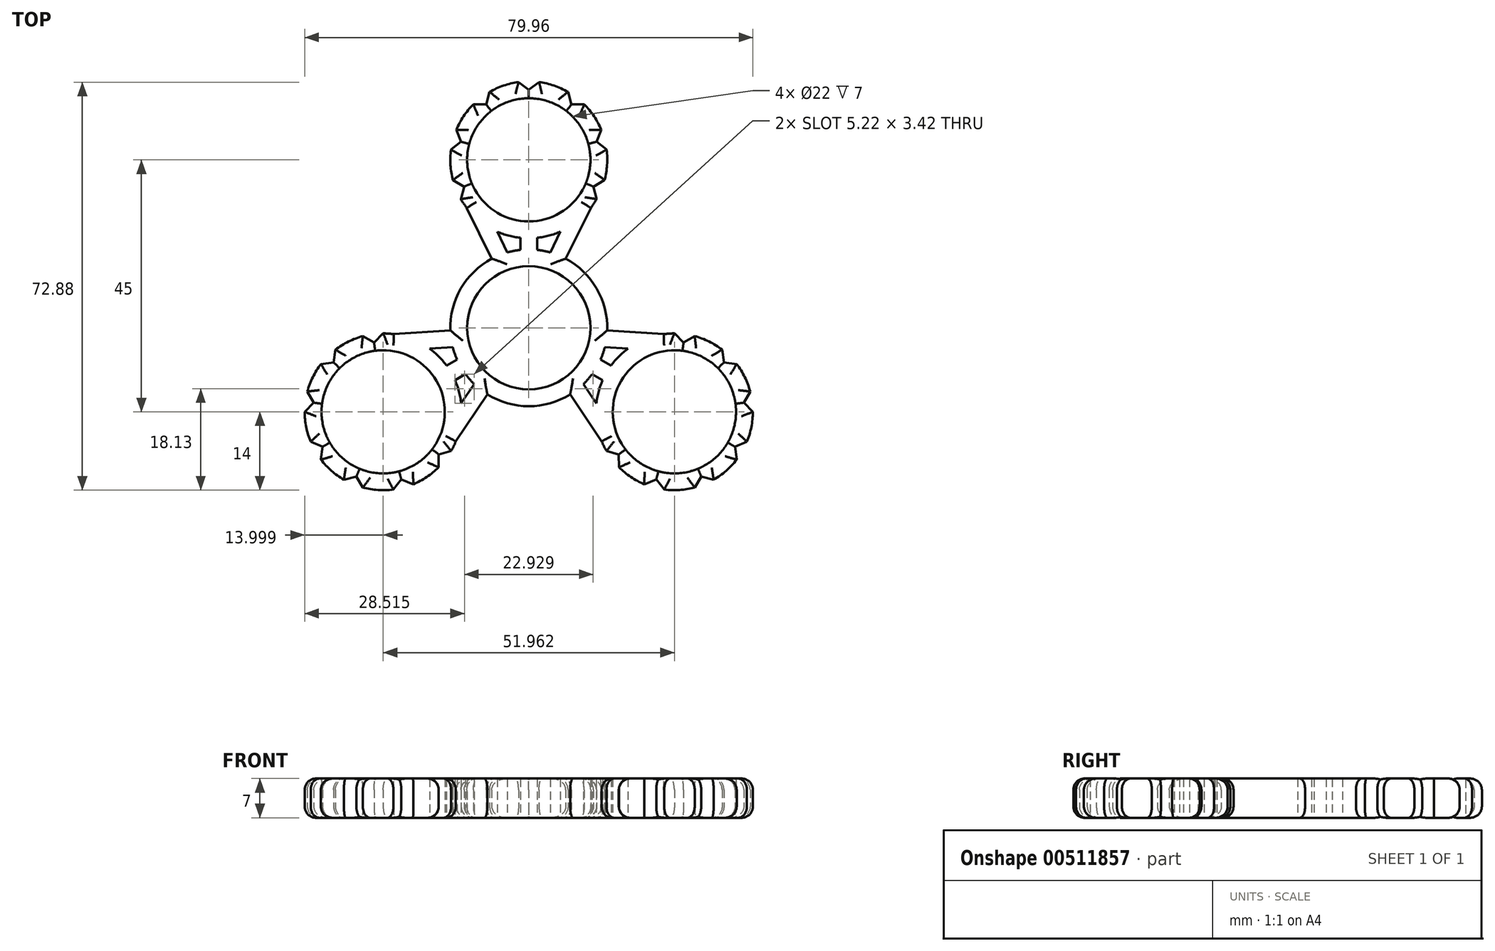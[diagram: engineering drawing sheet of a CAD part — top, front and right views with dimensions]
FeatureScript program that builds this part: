
annotation { "Feature Type Name" : "Feature", "Feature Type Description" : "" }
export const myFeature = defineFeature(function(context is Context, id is Id, definition is map)
    precondition{}
    {
        {
            var Q0;
            Q0=qCreatedBy(makeId("Top.planeOp"),FACE);
            var sketch = newSketch(context, id + "F0", { "sketchPlane" : qUnion([Q0])});
            skCircle(sketch, "E0", {"center": v(0, 0) * mm, "radius": 11 * mm});
            skCircle(sketch, "E1", {"center": v(0, 30) * mm, "radius": 11 * mm});
            skArc(sketch, "E2.0", {"start": v(-3.45, 16.43) * mm, "mid": v(9.84, 39.96) * mm, "end": v(-13.52, 26.38) * mm});
            skCircle(sketch, "E3.0", {"center": v(0, 0) * mm, "radius": 14 * mm});
            skLineSegment(sketch, "E4", {"start": v(-1.5, 15) * mm, "end": v(-1.5, 13.92) * mm});
            skLineSegment(sketch, "E5", {"start": v(-1.5, 15) * mm, "end": v(-1.5, 16.08) * mm});
            skPoint(sketch, "E6.MirrorCS.start.orphan", {"position": v(0, 15) * mm});
            skPoint(sketch, "E7.orphan", {"position": v(0, 16) * mm});
            skPoint(sketch, "E8.start.orphan", {"position": v(0, 14) * mm});
            skLineSegment(sketch, "E9.MirrorCS", {"start": v(1.5, 15) * mm, "end": v(1.5, 16.08) * mm});
            skLineSegment(sketch, "E10.MirrorCS", {"start": v(1.5, 15) * mm, "end": v(1.5, 13.92) * mm});
            skLineSegment(sketch, "E11", {"start": v(-9.53, 24.5) * mm, "end": v(-12.12, 23) * mm});
            skLineSegment(sketch, "E12", {"start": v(-10.63, 27.15) * mm, "end": v(-13.52, 26.38) * mm});
            skLineSegment(sketch, "E13", {"start": v(-12.12, 23) * mm, "end": v(-11.55, 25.22) * mm});
            skLineSegment(sketch, "E14", {"start": v(-11.55, 25.22) * mm, "end": v(-13.52, 26.38) * mm});
            skArc(sketch, "E15.trimOffspring", {"start": v(-12.12, 23) * mm, "mid": v(-11.62, 22.19) * mm, "end": v(-11.05, 21.4) * mm});
            skPoint(sketch, "E16.orphan", {"position": v(-12.93, 24.64) * mm});
            skPoint(sketch, "E17.start.orphan", {"position": v(-10.16, 25.8) * mm});
            skLineSegment(sketch, "E18.MirrorCS", {"start": v(9.53, 24.5) * mm, "end": v(12.12, 23) * mm});
            skLineSegment(sketch, "E19.1.0", {"start": v(-13.88, 31.83) * mm, "end": v(-12.07, 33.24) * mm});
            skLineSegment(sketch, "E19.1.1", {"start": v(-12.07, 33.24) * mm, "end": v(-12.93, 35.36) * mm});
            skLineSegment(sketch, "E19.2.0", {"start": v(-9.9, 39.9) * mm, "end": v(-7.6, 39.92) * mm});
            skLineSegment(sketch, "E19.2.1", {"start": v(-7.6, 39.92) * mm, "end": v(-7, 42.12) * mm});
            skLineSegment(sketch, "E19.3.0", {"start": v(-1.83, 43.88) * mm, "end": v(0, 42.5) * mm});
            skLineSegment(sketch, "E19.3.1", {"start": v(0, 42.5) * mm, "end": v(1.83, 43.88) * mm});
            skLineSegment(sketch, "E19.4.0", {"start": v(7, 42.12) * mm, "end": v(7.6, 39.92) * mm});
            skLineSegment(sketch, "E19.4.1", {"start": v(7.6, 39.92) * mm, "end": v(9.9, 39.9) * mm});
            skLineSegment(sketch, "E19.5.0", {"start": v(12.93, 35.36) * mm, "end": v(12.07, 33.24) * mm});
            skLineSegment(sketch, "E19.5.1", {"start": v(12.07, 33.24) * mm, "end": v(13.88, 31.83) * mm});
            skLineSegment(sketch, "E19.6.0", {"start": v(13.52, 26.38) * mm, "end": v(11.55, 25.22) * mm});
            skLineSegment(sketch, "E19.6.1", {"start": v(11.55, 25.22) * mm, "end": v(12.12, 23) * mm});
            skLineSegment(sketch, "E19.anchor1", {"start": v(0, 30) * mm, "end": v(-12.12, 23) * mm, "construction": true});
            skLineSegment(sketch, "E19.anchor2", {"start": v(0, 30) * mm, "end": v(13.52, 26.38) * mm, "construction": true});
            skLineSegment(sketch, "E20.MirrorCS", {"start": v(11.05, 21.4) * mm, "end": v(6.6, 12.34) * mm});
            skPoint(sketch, "E21.MirrorCS.end.orphan", {"position": v(11.05, 21.4) * mm});
            skPoint(sketch, "E21.MirrorCS.start.orphan", {"position": v(4.67, 13.2) * mm});
            skLineSegment(sketch, "E22", {"start": v(3.82, 13.47) * mm, "end": v(5.64, 17.19) * mm});
            skPoint(sketch, "E23.start.orphan", {"position": v(-4.67, 13.2) * mm});
            skPoint(sketch, "E24.end.orphan", {"position": v(-6.6, 12.34) * mm});
            skArc(sketch, "E25", {"start": v(-11.05, 21.4) * mm, "mid": v(-7.67, 18.29) * mm, "end": v(-3.45, 16.43) * mm});
            skLineSegment(sketch, "E26.MirrorCS", {"start": v(-3.82, 13.47) * mm, "end": v(-5.64, 17.19) * mm});
            skLineSegment(sketch, "E27.MirrorCS", {"start": v(-11.05, 21.4) * mm, "end": v(-6.6, 12.34) * mm});
            skPoint(sketch, "E28.MirrorCS.end.orphan", {"position": v(3.45, 16.43) * mm});
            skPoint(sketch, "E28.MirrorCS.start.orphan", {"position": v(1.5, 13.92) * mm});
            skLineSegment(sketch, "E29.1.0", {"start": v(-24.07, -1.13) * mm, "end": v(-14, -0.45) * mm});
            skLineSegment(sketch, "E29.1.1", {"start": v(-13.57, -3.42) * mm, "end": v(-17.7, -3.7) * mm});
            skArc(sketch, "E29.1.2", {"start": v(-12.5, -11.2) * mm, "mid": v(-39.53, -11.46) * mm, "end": v(-16.08, -24.9) * mm});
            skLineSegment(sketch, "E29.1.3", {"start": v(-13.74, -6.2) * mm, "end": v(-12.8, -5.66) * mm});
            skLineSegment(sketch, "E29.1.4", {"start": v(-13.74, -6.2) * mm, "end": v(-14.68, -6.74) * mm});
            skLineSegment(sketch, "E29.1.5", {"start": v(-12.24, -8.8) * mm, "end": v(-13.18, -9.34) * mm});
            skLineSegment(sketch, "E29.1.6", {"start": v(-12.24, -8.8) * mm, "end": v(-11.3, -8.26) * mm});
            skArc(sketch, "E29.1.7", {"start": v(-13.01, -20.28) * mm, "mid": v(-12, -15.78) * mm, "end": v(-12.5, -11.2) * mm});
            skLineSegment(sketch, "E29.1.8", {"start": v(-13.01, -20.28) * mm, "end": v(-7.38, -11.9) * mm});
            skLineSegment(sketch, "E29.1.9", {"start": v(-9.75, -10.04) * mm, "end": v(-12.06, -13.48) * mm});
            skLineSegment(sketch, "E29.1.10", {"start": v(-13.86, -22) * mm, "end": v(-16.06, -22.6) * mm});
            skLineSegment(sketch, "E29.1.11", {"start": v(-16.06, -22.6) * mm, "end": v(-16.08, -24.9) * mm});
            skLineSegment(sketch, "E29.1.12", {"start": v(-20.62, -27.93) * mm, "end": v(-22.75, -27.07) * mm});
            skLineSegment(sketch, "E29.1.13", {"start": v(-22.75, -27.07) * mm, "end": v(-24.15, -28.88) * mm});
            skLineSegment(sketch, "E29.1.14", {"start": v(-29.6, -28.52) * mm, "end": v(-30.76, -26.55) * mm});
            skLineSegment(sketch, "E29.1.15", {"start": v(-30.76, -26.55) * mm, "end": v(-32.98, -27.12) * mm});
            skLineSegment(sketch, "E29.1.16", {"start": v(-36.8, -21.25) * mm, "end": v(-38.92, -20.36) * mm});
            skLineSegment(sketch, "E29.1.17", {"start": v(-37.09, -23.52) * mm, "end": v(-36.8, -21.25) * mm});
            skCircle(sketch, "E29.1.18", {"center": v(-25.98, -15) * mm, "radius": 11 * mm});
            skLineSegment(sketch, "E29.1.19", {"start": v(-38.37, -13.37) * mm, "end": v(-39.5, -11.38) * mm});
            skLineSegment(sketch, "E29.1.20", {"start": v(-39.98, -15) * mm, "end": v(-38.37, -13.37) * mm});
            skLineSegment(sketch, "E29.1.21", {"start": v(-37.09, -6.48) * mm, "end": v(-34.82, -6.16) * mm});
            skLineSegment(sketch, "E29.1.22", {"start": v(-34.82, -6.16) * mm, "end": v(-34.5, -3.9) * mm});
            skLineSegment(sketch, "E29.1.23", {"start": v(-29.6, -1.48) * mm, "end": v(-27.61, -2.6) * mm});
            skLineSegment(sketch, "E29.1.24", {"start": v(-27.61, -2.6) * mm, "end": v(-25.98, -1) * mm});
            skArc(sketch, "E29.1.25", {"start": v(-13.86, -22) * mm, "mid": v(-13.4, -21.15) * mm, "end": v(-13.01, -20.28) * mm});
            skLineSegment(sketch, "E29.2.0", {"start": v(13.01, -20.28) * mm, "end": v(7.38, -11.9) * mm});
            skLineSegment(sketch, "E29.2.1", {"start": v(9.75, -10.04) * mm, "end": v(12.06, -13.48) * mm});
            skArc(sketch, "E29.2.2", {"start": v(15.96, -5.23) * mm, "mid": v(29.69, -28.5) * mm, "end": v(29.6, -1.48) * mm});
            skLineSegment(sketch, "E29.2.3", {"start": v(12.24, -8.8) * mm, "end": v(11.3, -8.26) * mm});
            skLineSegment(sketch, "E29.2.4", {"start": v(12.24, -8.8) * mm, "end": v(13.18, -9.34) * mm});
            skLineSegment(sketch, "E29.2.5", {"start": v(13.74, -6.2) * mm, "end": v(14.68, -6.74) * mm});
            skLineSegment(sketch, "E29.2.6", {"start": v(13.74, -6.2) * mm, "end": v(12.8, -5.66) * mm});
            skArc(sketch, "E29.2.7", {"start": v(24.07, -1.13) * mm, "mid": v(19.67, -2.5) * mm, "end": v(15.96, -5.23) * mm});
            skLineSegment(sketch, "E29.2.8", {"start": v(24.07, -1.13) * mm, "end": v(14, -0.45) * mm});
            skLineSegment(sketch, "E29.2.9", {"start": v(13.57, -3.42) * mm, "end": v(17.7, -3.7) * mm});
            skLineSegment(sketch, "E29.2.10", {"start": v(25.98, -1) * mm, "end": v(27.61, -2.6) * mm});
            skLineSegment(sketch, "E29.2.11", {"start": v(27.61, -2.6) * mm, "end": v(29.6, -1.48) * mm});
            skLineSegment(sketch, "E29.2.12", {"start": v(34.5, -3.9) * mm, "end": v(34.82, -6.16) * mm});
            skLineSegment(sketch, "E29.2.13", {"start": v(34.82, -6.16) * mm, "end": v(37.09, -6.48) * mm});
            skLineSegment(sketch, "E29.2.14", {"start": v(39.5, -11.38) * mm, "end": v(38.37, -13.37) * mm});
            skLineSegment(sketch, "E29.2.15", {"start": v(38.37, -13.37) * mm, "end": v(39.98, -15) * mm});
            skLineSegment(sketch, "E29.2.16", {"start": v(36.8, -21.25) * mm, "end": v(37.09, -23.52) * mm});
            skLineSegment(sketch, "E29.2.17", {"start": v(38.92, -20.36) * mm, "end": v(36.8, -21.25) * mm});
            skCircle(sketch, "E29.2.18", {"center": v(25.98, -15) * mm, "radius": 11 * mm});
            skLineSegment(sketch, "E29.2.19", {"start": v(30.76, -26.55) * mm, "end": v(29.6, -28.52) * mm});
            skLineSegment(sketch, "E29.2.20", {"start": v(32.98, -27.12) * mm, "end": v(30.76, -26.55) * mm});
            skLineSegment(sketch, "E29.2.21", {"start": v(24.15, -28.88) * mm, "end": v(22.75, -27.07) * mm});
            skLineSegment(sketch, "E29.2.22", {"start": v(22.75, -27.07) * mm, "end": v(20.62, -27.93) * mm});
            skLineSegment(sketch, "E29.2.23", {"start": v(16.08, -24.9) * mm, "end": v(16.06, -22.6) * mm});
            skLineSegment(sketch, "E29.2.24", {"start": v(16.06, -22.6) * mm, "end": v(13.86, -22) * mm});
            skArc(sketch, "E29.2.25", {"start": v(25.98, -1) * mm, "mid": v(25.02, -1.03) * mm, "end": v(24.07, -1.13) * mm});
            skSolve(sketch);
        }
        {
            var Q0;
            {var subQ1=sQuery(id+"F0.wireOp",EDGE,"E11");Q0=makeQuery(id+"F0.imprint","IMPRINT",FACE,{"disambiguationData":[TD([[makeQuery(id+"F0.imprint","IMPRINT",EDGE,{"derivedFrom":subQ1}),1.0]])]});}
            var Q1;
            {var subQ0=sQuery(id+"F0.wireOp",EDGE,"E11");Q1=makeQuery(id+"F0.imprint","IMPRINT",FACE,{"disambiguationData":[TD([[makeQuery(id+"F0.imprint","IMPRINT",EDGE,{"derivedFrom":subQ0}),-1.0]])]});}
            var Q2;
            {var subQ1=sQuery(id+"F0.wireOp",EDGE,"E12");Q2=makeQuery(id+"F0.imprint","IMPRINT",FACE,{"disambiguationData":[TD([[makeQuery(id+"F0.imprint","IMPRINT",EDGE,{"derivedFrom":subQ1}),-1.0]])]});}
            var Q3;
            {var subQ0=sQuery(id+"F0.wireOp",EDGE,"E20.MirrorCS");Q3=makeQuery(id+"F0.imprint","IMPRINT",FACE,{"disambiguationData":[TD([[makeQuery(id+"F0.imprint","IMPRINT",EDGE,{"derivedFrom":subQ0}),-1.0]])]});}
            var Q4;
            {var subQ0=sQuery(id+"F0.wireOp",EDGE,"E26.MirrorCS");Q4=makeQuery(id+"F0.imprint","IMPRINT",FACE,{"disambiguationData":[TD([[makeQuery(id+"F0.imprint","IMPRINT",EDGE,{"derivedFrom":subQ0}),1.0]])]});}
            var Q5;
            {var subQ0=sQuery(id+"F0.wireOp",EDGE,"E4");Q5=makeQuery(id+"F0.imprint","IMPRINT",FACE,{"disambiguationData":[TD([[makeQuery(id+"F0.imprint","IMPRINT",EDGE,{"derivedFrom":subQ0}),1.0]])]});}
            var Q6;
            Q6=makeQuery(id+"F0.imprint","IMPRINT",FACE,{"disambiguationData":[TD([[makeQuery(id+"F0.imprint","IMPRINT",EDGE,{"derivedFrom":sQuery(id+"F0.wireOp",EDGE,"E0")}),-1.0]])]});
            var Q7;
            {var subQ0=sQuery(id+"F0.wireOp",EDGE,"E29.1.0");Q7=makeQuery(id+"F0.imprint","IMPRINT",FACE,{"disambiguationData":[TD([[makeQuery(id+"F0.imprint","IMPRINT",EDGE,{"derivedFrom":subQ0}),-1.0]])]});}
            var Q8;
            {var subQ1=sQuery(id+"F0.wireOp",EDGE,"E29.1.3");Q8=makeQuery(id+"F0.imprint","IMPRINT",FACE,{"disambiguationData":[TD([[makeQuery(id+"F0.imprint","IMPRINT",EDGE,{"derivedFrom":subQ1}),-1.0]])]});}
            var Q9;
            {var subQ0=sQuery(id+"F0.wireOp",EDGE,"E29.1.8");Q9=makeQuery(id+"F0.imprint","IMPRINT",FACE,{"disambiguationData":[TD([[makeQuery(id+"F0.imprint","IMPRINT",EDGE,{"derivedFrom":subQ0}),1.0]])]});}
            var Q10;
            Q10=makeQuery(id+"F0.imprint","IMPRINT",FACE,{"disambiguationData":[TD([[makeQuery(id+"F0.imprint","IMPRINT",EDGE,{"derivedFrom":sQuery(id+"F0.wireOp",EDGE,"E29.1.10")}),-1.0]])]});
            var Q11;
            {var subQ0=sQuery(id+"F0.wireOp",EDGE,"E29.2.0");Q11=makeQuery(id+"F0.imprint","IMPRINT",FACE,{"disambiguationData":[TD([[makeQuery(id+"F0.imprint","IMPRINT",EDGE,{"derivedFrom":subQ0}),-1.0]])]});}
            var Q12;
            {var subQ0=sQuery(id+"F0.wireOp",EDGE,"E29.2.3");Q12=makeQuery(id+"F0.imprint","IMPRINT",FACE,{"disambiguationData":[TD([[makeQuery(id+"F0.imprint","IMPRINT",EDGE,{"derivedFrom":subQ0}),-1.0]])]});}
            var Q13;
            {var subQ0=sQuery(id+"F0.wireOp",EDGE,"E29.2.8");Q13=makeQuery(id+"F0.imprint","IMPRINT",FACE,{"disambiguationData":[TD([[makeQuery(id+"F0.imprint","IMPRINT",EDGE,{"derivedFrom":subQ0}),1.0]])]});}
            var Q14;
            Q14=makeQuery(id+"F0.imprint","IMPRINT",FACE,{"disambiguationData":[TD([[makeQuery(id+"F0.imprint","IMPRINT",EDGE,{"derivedFrom":sQuery(id+"F0.wireOp",EDGE,"E29.2.10")}),-1.0]])]});
            extrude(context, id + "F1", {"entities" : qUnion([Q0, Q1, Q2, Q3, Q4, Q5, Q6, Q7, Q8, Q9, Q10, Q11, Q12, Q13, Q14]), "depth" : 7 * mm});
        }
        {
            var Q0;
            Q0=makeQuery(id+"F1.opExtrude","CAP_EDGE",EDGE,{"disambiguationData":[OSD([sQuery(id+"F0.wireOp",EDGE,"E20.MirrorCS")])],"isStart":false});
            var Q1;
            Q1=makeQuery(id+"F1.opExtrude","CAP_EDGE",EDGE,{"disambiguationData":[OSD([sQuery(id+"F0.wireOp",EDGE,"E19.6.1")])],"isStart":false});
            var Q2;
            {var subQ0=sQuery(id+"F0.wireOp",EDGE,"E2.0");Q2=makeQuery(id+"F1.opExtrude","CAP_EDGE",EDGE,{"disambiguationData":[OSD([subQ0]),TDD([makeQuery(id+"F0.imprint","IMPRINT",EDGE,{"disambiguationData":[TD([[makeQuery(id+"F0.imprint","INTERSECT",VERTEX,{"derivedFrom":[subQ0,sQuery(id+"F0.wireOp",EDGE,"E20.MirrorCS")]}),-1.0]])],"derivedFrom":subQ0})])],"isStart":false});}
            var Q3;
            Q3=makeQuery(id+"F1.opExtrude","CAP_EDGE",EDGE,{"disambiguationData":[OSD([sQuery(id+"F0.wireOp",EDGE,"E19.6.0")])],"isStart":false});
            var Q4;
            {var subQ0=sQuery(id+"F0.wireOp",EDGE,"E2.0");Q4=makeQuery(id+"F1.opExtrude","CAP_EDGE",EDGE,{"disambiguationData":[OSD([subQ0]),TDD([makeQuery(id+"F0.imprint","IMPRINT",EDGE,{"disambiguationData":[TD([[makeQuery(id+"F0.imprint","INTERSECT",VERTEX,{"derivedFrom":[subQ0,sQuery(id+"F0.wireOp",EDGE,"E19.5.1")]}),1.0]])],"derivedFrom":subQ0})])],"isStart":false});}
            var Q5;
            Q5=makeQuery(id+"F1.opExtrude","CAP_EDGE",EDGE,{"disambiguationData":[OSD([sQuery(id+"F0.wireOp",EDGE,"E19.5.1")])],"isStart":false});
            var Q6;
            Q6=makeQuery(id+"F1.opExtrude","CAP_EDGE",EDGE,{"disambiguationData":[OSD([sQuery(id+"F0.wireOp",EDGE,"E19.5.0")])],"isStart":false});
            var Q7;
            {var subQ0=sQuery(id+"F0.wireOp",EDGE,"E2.0");Q7=makeQuery(id+"F1.opExtrude","CAP_EDGE",EDGE,{"disambiguationData":[OSD([subQ0]),TDD([makeQuery(id+"F0.imprint","IMPRINT",EDGE,{"disambiguationData":[TD([[makeQuery(id+"F0.imprint","INTERSECT",VERTEX,{"derivedFrom":[subQ0,sQuery(id+"F0.wireOp",EDGE,"E19.4.1")]}),1.0]])],"derivedFrom":subQ0})])],"isStart":false});}
            var Q8;
            Q8=makeQuery(id+"F1.opExtrude","CAP_EDGE",EDGE,{"disambiguationData":[OSD([sQuery(id+"F0.wireOp",EDGE,"E19.4.1")])],"isStart":false});
            var Q9;
            Q9=makeQuery(id+"F1.opExtrude","CAP_EDGE",EDGE,{"disambiguationData":[OSD([sQuery(id+"F0.wireOp",EDGE,"E19.4.0")])],"isStart":false});
            var Q10;
            {var subQ0=sQuery(id+"F0.wireOp",EDGE,"E2.0");Q10=makeQuery(id+"F1.opExtrude","CAP_EDGE",EDGE,{"disambiguationData":[OSD([subQ0]),TDD([makeQuery(id+"F0.imprint","IMPRINT",EDGE,{"disambiguationData":[TD([[makeQuery(id+"F0.imprint","INTERSECT",VERTEX,{"derivedFrom":[subQ0,sQuery(id+"F0.wireOp",EDGE,"E19.3.1")]}),1.0]])],"derivedFrom":subQ0})])],"isStart":false});}
            var Q11;
            Q11=makeQuery(id+"F1.opExtrude","CAP_EDGE",EDGE,{"disambiguationData":[OSD([sQuery(id+"F0.wireOp",EDGE,"E19.3.0")])],"isStart":false});
            var Q12;
            {var subQ0=sQuery(id+"F0.wireOp",EDGE,"E2.0");Q12=makeQuery(id+"F1.opExtrude","CAP_EDGE",EDGE,{"disambiguationData":[OSD([subQ0]),TDD([makeQuery(id+"F0.imprint","IMPRINT",EDGE,{"disambiguationData":[TD([[makeQuery(id+"F0.imprint","INTERSECT",VERTEX,{"derivedFrom":[subQ0,sQuery(id+"F0.wireOp",EDGE,"E19.2.1")]}),1.0]])],"derivedFrom":subQ0})])],"isStart":false});}
            var Q13;
            Q13=makeQuery(id+"F1.opExtrude","CAP_EDGE",EDGE,{"disambiguationData":[OSD([sQuery(id+"F0.wireOp",EDGE,"E19.2.1")])],"isStart":false});
            var Q14;
            Q14=makeQuery(id+"F1.opExtrude","CAP_EDGE",EDGE,{"disambiguationData":[OSD([sQuery(id+"F0.wireOp",EDGE,"E19.2.0")])],"isStart":false});
            var Q15;
            {var subQ0=sQuery(id+"F0.wireOp",EDGE,"E2.0");Q15=makeQuery(id+"F1.opExtrude","CAP_EDGE",EDGE,{"disambiguationData":[OSD([subQ0]),TDD([makeQuery(id+"F0.imprint","IMPRINT",EDGE,{"disambiguationData":[TD([[makeQuery(id+"F0.imprint","INTERSECT",VERTEX,{"derivedFrom":[subQ0,sQuery(id+"F0.wireOp",EDGE,"E19.1.1")]}),1.0]])],"derivedFrom":subQ0})])],"isStart":false});}
            var Q16;
            {var subQ0=sQuery(id+"F0.wireOp",EDGE,"E2.0");Q16=makeQuery(id+"F1.opExtrude","CAP_EDGE",EDGE,{"disambiguationData":[OSD([subQ0]),TDD([makeQuery(id+"F0.imprint","IMPRINT",EDGE,{"disambiguationData":[TD([[makeQuery(id+"F0.imprint","INTERSECT",VERTEX,{"derivedFrom":[subQ0,sQuery(id+"F0.wireOp",EDGE,"E19.1.0")]}),-1.0]])],"derivedFrom":subQ0})])],"isStart":false});}
            var Q17;
            Q17=makeQuery(id+"F1.opExtrude","CAP_EDGE",EDGE,{"disambiguationData":[OSD([sQuery(id+"F0.wireOp",EDGE,"E19.1.0")])],"isStart":false});
            var Q18;
            Q18=makeQuery(id+"F1.opExtrude","CAP_EDGE",EDGE,{"disambiguationData":[OSD([sQuery(id+"F0.wireOp",EDGE,"E19.1.1")])],"isStart":false});
            var Q19;
            Q19=makeQuery(id+"F1.opExtrude","CAP_EDGE",EDGE,{"disambiguationData":[OSD([sQuery(id+"F0.wireOp",EDGE,"E14")])],"isStart":false});
            var Q20;
            Q20=makeQuery(id+"F1.opExtrude","CAP_EDGE",EDGE,{"disambiguationData":[OSD([sQuery(id+"F0.wireOp",EDGE,"E13")])],"isStart":false});
            var Q21;
            Q21=makeQuery(id+"F1.opExtrude","CAP_EDGE",EDGE,{"disambiguationData":[OSD([sQuery(id+"F0.wireOp",EDGE,"E27.MirrorCS")])],"isStart":false});
            var Q22;
            Q22=makeQuery(id+"F1.opExtrude","CAP_EDGE",EDGE,{"disambiguationData":[OSD([sQuery(id+"F0.wireOp",EDGE,"E15.trimOffspring")])],"isStart":false});
            var Q23;
            {var subQ0=sQuery(id+"F0.wireOp",EDGE,"E3.0");Q23=makeQuery(id+"F1.opExtrude","CAP_EDGE",EDGE,{"disambiguationData":[OSD([subQ0]),TDD([makeQuery(id+"F0.imprint","IMPRINT",EDGE,{"disambiguationData":[TD([[makeQuery(id+"F0.imprint","INTERSECT",VERTEX,{"derivedFrom":[subQ0,sQuery(id+"F0.wireOp",EDGE,"E27.MirrorCS")]}),-1.0]])],"derivedFrom":subQ0})])],"isStart":false});}
            var Q24;
            Q24=makeQuery(id+"F1.opExtrude","CAP_EDGE",EDGE,{"disambiguationData":[OSD([sQuery(id+"F0.wireOp",EDGE,"E29.1.0")])],"isStart":false});
            var Q25;
            {var subQ0=sQuery(id+"F0.wireOp",EDGE,"E29.1.2");Q25=makeQuery(id+"F1.opExtrude","CAP_EDGE",EDGE,{"disambiguationData":[OSD([subQ0]),TDD([makeQuery(id+"F0.imprint","IMPRINT",EDGE,{"disambiguationData":[TD([[makeQuery(id+"F0.imprint","INTERSECT",VERTEX,{"derivedFrom":[sQuery(id+"F0.wireOp",EDGE,"E29.1.0"),subQ0]}),-1.0]])],"derivedFrom":subQ0})])],"isStart":false});}
            var Q26;
            Q26=makeQuery(id+"F1.opExtrude","CAP_EDGE",EDGE,{"disambiguationData":[OSD([sQuery(id+"F0.wireOp",EDGE,"E29.1.24")])],"isStart":false});
            var Q27;
            Q27=makeQuery(id+"F1.opExtrude","CAP_EDGE",EDGE,{"disambiguationData":[OSD([sQuery(id+"F0.wireOp",EDGE,"E29.1.23")])],"isStart":false});
            var Q28;
            {var subQ0=sQuery(id+"F0.wireOp",EDGE,"E29.1.2");Q28=makeQuery(id+"F1.opExtrude","CAP_EDGE",EDGE,{"disambiguationData":[OSD([subQ0]),TDD([makeQuery(id+"F0.imprint","IMPRINT",EDGE,{"disambiguationData":[TD([[makeQuery(id+"F0.imprint","INTERSECT",VERTEX,{"derivedFrom":[subQ0,sQuery(id+"F0.wireOp",EDGE,"E29.1.22")]}),1.0]])],"derivedFrom":subQ0})])],"isStart":false});}
            var Q29;
            {var subQ0=sQuery(id+"F0.wireOp",EDGE,"E29.1.2");Q29=makeQuery(id+"F1.opExtrude","CAP_EDGE",EDGE,{"disambiguationData":[OSD([subQ0]),TDD([makeQuery(id+"F0.imprint","IMPRINT",EDGE,{"disambiguationData":[TD([[makeQuery(id+"F0.imprint","INTERSECT",VERTEX,{"derivedFrom":[subQ0,sQuery(id+"F0.wireOp",EDGE,"E29.1.19")]}),1.0]])],"derivedFrom":subQ0})])],"isStart":false});}
            var Q30;
            Q30=makeQuery(id+"F1.opExtrude","CAP_EDGE",EDGE,{"disambiguationData":[OSD([sQuery(id+"F0.wireOp",EDGE,"E29.1.19")])],"isStart":false});
            var Q31;
            Q31=makeQuery(id+"F1.opExtrude","CAP_EDGE",EDGE,{"disambiguationData":[OSD([sQuery(id+"F0.wireOp",EDGE,"E29.1.20")])],"isStart":false});
            var Q32;
            {var subQ0=sQuery(id+"F0.wireOp",EDGE,"E29.1.2");Q32=makeQuery(id+"F1.opExtrude","CAP_EDGE",EDGE,{"disambiguationData":[OSD([subQ0]),TDD([makeQuery(id+"F0.imprint","IMPRINT",EDGE,{"disambiguationData":[TD([[makeQuery(id+"F0.imprint","INTERSECT",VERTEX,{"derivedFrom":[subQ0,sQuery(id+"F0.wireOp",EDGE,"E29.1.16")]}),1.0]])],"derivedFrom":subQ0})])],"isStart":false});}
            var Q33;
            Q33=makeQuery(id+"F1.opExtrude","CAP_EDGE",EDGE,{"disambiguationData":[OSD([sQuery(id+"F0.wireOp",EDGE,"E29.1.21")])],"isStart":false});
            var Q34;
            Q34=makeQuery(id+"F1.opExtrude","CAP_EDGE",EDGE,{"disambiguationData":[OSD([sQuery(id+"F0.wireOp",EDGE,"E29.1.22")])],"isStart":false});
            var Q35;
            Q35=makeQuery(id+"F1.opExtrude","CAP_EDGE",EDGE,{"disambiguationData":[OSD([sQuery(id+"F0.wireOp",EDGE,"E29.1.16")])],"isStart":false});
            var Q36;
            Q36=makeQuery(id+"F1.opExtrude","CAP_EDGE",EDGE,{"disambiguationData":[OSD([sQuery(id+"F0.wireOp",EDGE,"E29.1.17")])],"isStart":false});
            var Q37;
            {var subQ0=sQuery(id+"F0.wireOp",EDGE,"E29.1.2");Q37=makeQuery(id+"F1.opExtrude","CAP_EDGE",EDGE,{"disambiguationData":[OSD([subQ0]),TDD([makeQuery(id+"F0.imprint","IMPRINT",EDGE,{"disambiguationData":[TD([[makeQuery(id+"F0.imprint","INTERSECT",VERTEX,{"derivedFrom":[subQ0,sQuery(id+"F0.wireOp",EDGE,"E29.1.15")]}),1.0]])],"derivedFrom":subQ0})])],"isStart":false});}
            var Q38;
            Q38=makeQuery(id+"F1.opExtrude","CAP_EDGE",EDGE,{"disambiguationData":[OSD([sQuery(id+"F0.wireOp",EDGE,"E29.1.15")])],"isStart":false});
            var Q39;
            Q39=makeQuery(id+"F1.opExtrude","CAP_EDGE",EDGE,{"disambiguationData":[OSD([sQuery(id+"F0.wireOp",EDGE,"E29.1.14")])],"isStart":false});
            var Q40;
            {var subQ0=sQuery(id+"F0.wireOp",EDGE,"E29.1.2");Q40=makeQuery(id+"F1.opExtrude","CAP_EDGE",EDGE,{"disambiguationData":[OSD([subQ0]),TDD([makeQuery(id+"F0.imprint","IMPRINT",EDGE,{"disambiguationData":[TD([[makeQuery(id+"F0.imprint","INTERSECT",VERTEX,{"derivedFrom":[subQ0,sQuery(id+"F0.wireOp",EDGE,"E29.1.13")]}),1.0]])],"derivedFrom":subQ0})])],"isStart":false});}
            var Q41;
            {var subQ0=sQuery(id+"F0.wireOp",EDGE,"E29.1.2");Q41=makeQuery(id+"F1.opExtrude","CAP_EDGE",EDGE,{"disambiguationData":[OSD([subQ0]),TDD([makeQuery(id+"F0.imprint","IMPRINT",EDGE,{"disambiguationData":[TD([[makeQuery(id+"F0.imprint","INTERSECT",VERTEX,{"derivedFrom":[subQ0,sQuery(id+"F0.wireOp",EDGE,"E29.1.11")]}),1.0]])],"derivedFrom":subQ0})])],"isStart":false});}
            var Q42;
            Q42=makeQuery(id+"F1.opExtrude","CAP_EDGE",EDGE,{"disambiguationData":[OSD([sQuery(id+"F0.wireOp",EDGE,"E29.1.11")])],"isStart":false});
            var Q43;
            Q43=makeQuery(id+"F1.opExtrude","CAP_EDGE",EDGE,{"disambiguationData":[OSD([sQuery(id+"F0.wireOp",EDGE,"E29.1.10")])],"isStart":false});
            var Q44;
            Q44=makeQuery(id+"F1.opExtrude","CAP_EDGE",EDGE,{"disambiguationData":[OSD([sQuery(id+"F0.wireOp",EDGE,"E29.1.25")])],"isStart":false});
            var Q45;
            Q45=makeQuery(id+"F1.opExtrude","CAP_EDGE",EDGE,{"disambiguationData":[OSD([sQuery(id+"F0.wireOp",EDGE,"E19.3.1")])],"isStart":false});
            var Q46;
            Q46=makeQuery(id+"F1.opExtrude","CAP_EDGE",EDGE,{"disambiguationData":[OSD([sQuery(id+"F0.wireOp",EDGE,"E29.1.8")])],"isStart":false});
            var Q47;
            Q47=makeQuery(id+"F1.opExtrude","CAP_EDGE",EDGE,{"disambiguationData":[OSD([sQuery(id+"F0.wireOp",EDGE,"E29.1.13")])],"isStart":false});
            var Q48;
            Q48=makeQuery(id+"F1.opExtrude","CAP_EDGE",EDGE,{"disambiguationData":[OSD([sQuery(id+"F0.wireOp",EDGE,"E29.1.12")])],"isStart":false});
            var Q49;
            {var subQ0=sQuery(id+"F0.wireOp",EDGE,"E3.0");Q49=makeQuery(id+"F1.opExtrude","CAP_EDGE",EDGE,{"disambiguationData":[OSD([subQ0]),TDD([makeQuery(id+"F0.imprint","IMPRINT",EDGE,{"disambiguationData":[TD([[makeQuery(id+"F0.imprint","INTERSECT",VERTEX,{"derivedFrom":[subQ0,sQuery(id+"F0.wireOp",EDGE,"E29.1.8")]}),-1.0]])],"derivedFrom":subQ0})])],"isStart":false});}
            var Q50;
            Q50=makeQuery(id+"F1.opExtrude","CAP_EDGE",EDGE,{"disambiguationData":[OSD([sQuery(id+"F0.wireOp",EDGE,"E29.2.0")])],"isStart":false});
            var Q51;
            Q51=makeQuery(id+"F1.opExtrude","CAP_EDGE",EDGE,{"disambiguationData":[OSD([sQuery(id+"F0.wireOp",EDGE,"E29.2.24")])],"isStart":false});
            var Q52;
            Q52=makeQuery(id+"F1.opExtrude","CAP_EDGE",EDGE,{"disambiguationData":[OSD([sQuery(id+"F0.wireOp",EDGE,"E29.2.22")])],"isStart":false});
            var Q53;
            {var subQ0=sQuery(id+"F0.wireOp",EDGE,"E29.2.2");Q53=makeQuery(id+"F1.opExtrude","CAP_EDGE",EDGE,{"disambiguationData":[OSD([subQ0]),TDD([makeQuery(id+"F0.imprint","IMPRINT",EDGE,{"disambiguationData":[TD([[makeQuery(id+"F0.imprint","INTERSECT",VERTEX,{"derivedFrom":[subQ0,sQuery(id+"F0.wireOp",EDGE,"E29.2.19")]}),1.0]])],"derivedFrom":subQ0})])],"isStart":false});}
            var Q54;
            Q54=makeQuery(id+"F1.opExtrude","CAP_EDGE",EDGE,{"disambiguationData":[OSD([sQuery(id+"F0.wireOp",EDGE,"E29.2.19")])],"isStart":false});
            var Q55;
            Q55=makeQuery(id+"F1.opExtrude","CAP_EDGE",EDGE,{"disambiguationData":[OSD([sQuery(id+"F0.wireOp",EDGE,"E29.2.20")])],"isStart":false});
            var Q56;
            {var subQ0=sQuery(id+"F0.wireOp",EDGE,"E29.2.2");Q56=makeQuery(id+"F1.opExtrude","CAP_EDGE",EDGE,{"disambiguationData":[OSD([subQ0]),TDD([makeQuery(id+"F0.imprint","IMPRINT",EDGE,{"disambiguationData":[TD([[makeQuery(id+"F0.imprint","INTERSECT",VERTEX,{"derivedFrom":[subQ0,sQuery(id+"F0.wireOp",EDGE,"E29.2.16")]}),1.0]])],"derivedFrom":subQ0})])],"isStart":false});}
            var Q57;
            Q57=makeQuery(id+"F1.opExtrude","CAP_EDGE",EDGE,{"disambiguationData":[OSD([sQuery(id+"F0.wireOp",EDGE,"E29.2.16")])],"isStart":false});
            var Q58;
            Q58=makeQuery(id+"F1.opExtrude","CAP_EDGE",EDGE,{"disambiguationData":[OSD([sQuery(id+"F0.wireOp",EDGE,"E29.2.17")])],"isStart":false});
            var Q59;
            {var subQ0=sQuery(id+"F0.wireOp",EDGE,"E29.2.2");Q59=makeQuery(id+"F1.opExtrude","CAP_EDGE",EDGE,{"disambiguationData":[OSD([subQ0]),TDD([makeQuery(id+"F0.imprint","IMPRINT",EDGE,{"disambiguationData":[TD([[makeQuery(id+"F0.imprint","INTERSECT",VERTEX,{"derivedFrom":[subQ0,sQuery(id+"F0.wireOp",EDGE,"E29.2.15")]}),1.0]])],"derivedFrom":subQ0})])],"isStart":false});}
            var Q60;
            {var subQ0=sQuery(id+"F0.wireOp",EDGE,"E29.2.2");Q60=makeQuery(id+"F1.opExtrude","CAP_EDGE",EDGE,{"disambiguationData":[OSD([subQ0]),TDD([makeQuery(id+"F0.imprint","IMPRINT",EDGE,{"disambiguationData":[TD([[makeQuery(id+"F0.imprint","INTERSECT",VERTEX,{"derivedFrom":[sQuery(id+"F0.wireOp",EDGE,"E29.2.0"),subQ0]}),-1.0]])],"derivedFrom":subQ0})])],"isStart":false});}
            var Q61;
            Q61=makeQuery(id+"F1.opExtrude","CAP_EDGE",EDGE,{"disambiguationData":[OSD([sQuery(id+"F0.wireOp",EDGE,"E29.2.23")])],"isStart":false});
            var Q62;
            Q62=makeQuery(id+"F1.opExtrude","CAP_EDGE",EDGE,{"disambiguationData":[OSD([sQuery(id+"F0.wireOp",EDGE,"E29.2.21")])],"isStart":false});
            var Q63;
            {var subQ0=sQuery(id+"F0.wireOp",EDGE,"E29.2.2");Q63=makeQuery(id+"F1.opExtrude","CAP_EDGE",EDGE,{"disambiguationData":[OSD([subQ0]),TDD([makeQuery(id+"F0.imprint","IMPRINT",EDGE,{"disambiguationData":[TD([[makeQuery(id+"F0.imprint","INTERSECT",VERTEX,{"derivedFrom":[subQ0,sQuery(id+"F0.wireOp",EDGE,"E29.2.22")]}),1.0]])],"derivedFrom":subQ0})])],"isStart":false});}
            var Q64;
            Q64=makeQuery(id+"F1.opExtrude","CAP_EDGE",EDGE,{"disambiguationData":[OSD([sQuery(id+"F0.wireOp",EDGE,"E29.2.15")])],"isStart":false});
            var Q65;
            Q65=makeQuery(id+"F1.opExtrude","CAP_EDGE",EDGE,{"disambiguationData":[OSD([sQuery(id+"F0.wireOp",EDGE,"E29.2.14")])],"isStart":false});
            var Q66;
            {var subQ0=sQuery(id+"F0.wireOp",EDGE,"E29.2.2");Q66=makeQuery(id+"F1.opExtrude","CAP_EDGE",EDGE,{"disambiguationData":[OSD([subQ0]),TDD([makeQuery(id+"F0.imprint","IMPRINT",EDGE,{"disambiguationData":[TD([[makeQuery(id+"F0.imprint","INTERSECT",VERTEX,{"derivedFrom":[subQ0,sQuery(id+"F0.wireOp",EDGE,"E29.2.13")]}),1.0]])],"derivedFrom":subQ0})])],"isStart":false});}
            var Q67;
            Q67=makeQuery(id+"F1.opExtrude","CAP_EDGE",EDGE,{"disambiguationData":[OSD([sQuery(id+"F0.wireOp",EDGE,"E29.2.13")])],"isStart":false});
            var Q68;
            Q68=makeQuery(id+"F1.opExtrude","CAP_EDGE",EDGE,{"disambiguationData":[OSD([sQuery(id+"F0.wireOp",EDGE,"E29.2.12")])],"isStart":false});
            var Q69;
            {var subQ0=sQuery(id+"F0.wireOp",EDGE,"E29.2.2");Q69=makeQuery(id+"F1.opExtrude","CAP_EDGE",EDGE,{"disambiguationData":[OSD([subQ0]),TDD([makeQuery(id+"F0.imprint","IMPRINT",EDGE,{"disambiguationData":[TD([[makeQuery(id+"F0.imprint","INTERSECT",VERTEX,{"derivedFrom":[subQ0,sQuery(id+"F0.wireOp",EDGE,"E29.2.11")]}),1.0]])],"derivedFrom":subQ0})])],"isStart":false});}
            var Q70;
            Q70=makeQuery(id+"F1.opExtrude","CAP_EDGE",EDGE,{"disambiguationData":[OSD([sQuery(id+"F0.wireOp",EDGE,"E29.2.11")])],"isStart":false});
            var Q71;
            Q71=makeQuery(id+"F1.opExtrude","CAP_EDGE",EDGE,{"disambiguationData":[OSD([sQuery(id+"F0.wireOp",EDGE,"E29.2.10")])],"isStart":false});
            var Q72;
            Q72=makeQuery(id+"F1.opExtrude","CAP_EDGE",EDGE,{"disambiguationData":[OSD([sQuery(id+"F0.wireOp",EDGE,"E29.2.25")])],"isStart":false});
            var Q73;
            Q73=makeQuery(id+"F1.opExtrude","CAP_EDGE",EDGE,{"disambiguationData":[OSD([sQuery(id+"F0.wireOp",EDGE,"E29.2.8")])],"isStart":false});
            var Q74;
            {var subQ0=sQuery(id+"F0.wireOp",EDGE,"E3.0");Q74=makeQuery(id+"F1.opExtrude","CAP_EDGE",EDGE,{"disambiguationData":[OSD([subQ0]),TDD([makeQuery(id+"F0.imprint","IMPRINT",EDGE,{"disambiguationData":[TD([[makeQuery(id+"F0.imprint","INTERSECT",VERTEX,{"derivedFrom":[subQ0,sQuery(id+"F0.wireOp",EDGE,"E20.MirrorCS")]}),1.0]])],"derivedFrom":subQ0})])],"isStart":false});}
            fillet(context, id + "F2", {"entities" : qUnion([Q0, Q1, Q2, Q3, Q4, Q5, Q6, Q7, Q8, Q9, Q10, Q11, Q12, Q13, Q14, Q15, Q16, Q17, Q18, Q19, Q20, Q21, Q22, Q23, Q24, Q25, Q26, Q27, Q28, Q29, Q30, Q31, Q32, Q33, Q34, Q35, Q36, Q37, Q38, Q39, Q40, Q41, Q42, Q43, Q44, Q45, Q46, Q47, Q48, Q49, Q50, Q51, Q52, Q53, Q54, Q55, Q56, Q57, Q58, Q59, Q60, Q61, Q62, Q63, Q64, Q65, Q66, Q67, Q68, Q69, Q70, Q71, Q72, Q73, Q74]), "radius" : 2 * mm, "tangentPropagation" : true, "allowEdgeOverflow" : false});
        }
        {
            var Q0;
            Q0=makeQuery(id+"F1.opExtrude","CAP_EDGE",EDGE,{"disambiguationData":[OSD([sQuery(id+"F0.wireOp",EDGE,"E29.1.11")])],"isStart":true});
            var Q1;
            Q1=makeQuery(id+"F1.opExtrude","CAP_EDGE",EDGE,{"disambiguationData":[OSD([sQuery(id+"F0.wireOp",EDGE,"E29.1.10")])],"isStart":true});
            var Q2;
            Q2=makeQuery(id+"F1.opExtrude","CAP_EDGE",EDGE,{"disambiguationData":[OSD([sQuery(id+"F0.wireOp",EDGE,"E29.1.25")])],"isStart":true});
            var Q3;
            Q3=makeQuery(id+"F1.opExtrude","CAP_EDGE",EDGE,{"disambiguationData":[OSD([sQuery(id+"F0.wireOp",EDGE,"E29.1.8")])],"isStart":true});
            var Q4;
            {var subQ0=sQuery(id+"F0.wireOp",EDGE,"E29.1.2");Q4=makeQuery(id+"F1.opExtrude","CAP_EDGE",EDGE,{"disambiguationData":[OSD([subQ0]),TDD([makeQuery(id+"F0.imprint","IMPRINT",EDGE,{"disambiguationData":[TD([[makeQuery(id+"F0.imprint","INTERSECT",VERTEX,{"derivedFrom":[subQ0,sQuery(id+"F0.wireOp",EDGE,"E29.1.11")]}),1.0]])],"derivedFrom":subQ0})])],"isStart":true});}
            var Q5;
            Q5=makeQuery(id+"F1.opExtrude","CAP_EDGE",EDGE,{"disambiguationData":[OSD([sQuery(id+"F0.wireOp",EDGE,"E29.1.12")])],"isStart":true});
            var Q6;
            Q6=makeQuery(id+"F1.opExtrude","CAP_EDGE",EDGE,{"disambiguationData":[OSD([sQuery(id+"F0.wireOp",EDGE,"E29.1.13")])],"isStart":true});
            var Q7;
            {var subQ0=sQuery(id+"F0.wireOp",EDGE,"E29.1.2");Q7=makeQuery(id+"F1.opExtrude","CAP_EDGE",EDGE,{"disambiguationData":[OSD([subQ0]),TDD([makeQuery(id+"F0.imprint","IMPRINT",EDGE,{"disambiguationData":[TD([[makeQuery(id+"F0.imprint","INTERSECT",VERTEX,{"derivedFrom":[subQ0,sQuery(id+"F0.wireOp",EDGE,"E29.1.13")]}),1.0]])],"derivedFrom":subQ0})])],"isStart":true});}
            var Q8;
            Q8=makeQuery(id+"F1.opExtrude","CAP_EDGE",EDGE,{"disambiguationData":[OSD([sQuery(id+"F0.wireOp",EDGE,"E29.1.14")])],"isStart":true});
            var Q9;
            Q9=makeQuery(id+"F1.opExtrude","CAP_EDGE",EDGE,{"disambiguationData":[OSD([sQuery(id+"F0.wireOp",EDGE,"E29.1.15")])],"isStart":true});
            var Q10;
            Q10=makeQuery(id+"F1.opExtrude","CAP_EDGE",EDGE,{"disambiguationData":[OSD([sQuery(id+"F0.wireOp",EDGE,"E29.1.16")])],"isStart":true});
            var Q11;
            {var subQ0=sQuery(id+"F0.wireOp",EDGE,"E29.1.2");Q11=makeQuery(id+"F1.opExtrude","CAP_EDGE",EDGE,{"disambiguationData":[OSD([subQ0]),TDD([makeQuery(id+"F0.imprint","IMPRINT",EDGE,{"disambiguationData":[TD([[makeQuery(id+"F0.imprint","INTERSECT",VERTEX,{"derivedFrom":[subQ0,sQuery(id+"F0.wireOp",EDGE,"E29.1.16")]}),1.0]])],"derivedFrom":subQ0})])],"isStart":true});}
            var Q12;
            Q12=makeQuery(id+"F1.opExtrude","CAP_EDGE",EDGE,{"disambiguationData":[OSD([sQuery(id+"F0.wireOp",EDGE,"E29.1.20")])],"isStart":true});
            var Q13;
            Q13=makeQuery(id+"F1.opExtrude","CAP_EDGE",EDGE,{"disambiguationData":[OSD([sQuery(id+"F0.wireOp",EDGE,"E29.1.19")])],"isStart":true});
            var Q14;
            {var subQ0=sQuery(id+"F0.wireOp",EDGE,"E29.1.2");Q14=makeQuery(id+"F1.opExtrude","CAP_EDGE",EDGE,{"disambiguationData":[OSD([subQ0]),TDD([makeQuery(id+"F0.imprint","IMPRINT",EDGE,{"disambiguationData":[TD([[makeQuery(id+"F0.imprint","INTERSECT",VERTEX,{"derivedFrom":[subQ0,sQuery(id+"F0.wireOp",EDGE,"E29.1.19")]}),1.0]])],"derivedFrom":subQ0})])],"isStart":true});}
            var Q15;
            Q15=makeQuery(id+"F1.opExtrude","CAP_EDGE",EDGE,{"disambiguationData":[OSD([sQuery(id+"F0.wireOp",EDGE,"E29.1.21")])],"isStart":true});
            var Q16;
            Q16=makeQuery(id+"F1.opExtrude","CAP_EDGE",EDGE,{"disambiguationData":[OSD([sQuery(id+"F0.wireOp",EDGE,"E29.1.22")])],"isStart":true});
            var Q17;
            {var subQ0=sQuery(id+"F0.wireOp",EDGE,"E29.1.2");Q17=makeQuery(id+"F1.opExtrude","CAP_EDGE",EDGE,{"disambiguationData":[OSD([subQ0]),TDD([makeQuery(id+"F0.imprint","IMPRINT",EDGE,{"disambiguationData":[TD([[makeQuery(id+"F0.imprint","INTERSECT",VERTEX,{"derivedFrom":[subQ0,sQuery(id+"F0.wireOp",EDGE,"E29.1.22")]}),1.0]])],"derivedFrom":subQ0})])],"isStart":true});}
            var Q18;
            Q18=makeQuery(id+"F1.opExtrude","CAP_EDGE",EDGE,{"disambiguationData":[OSD([sQuery(id+"F0.wireOp",EDGE,"E29.1.23")])],"isStart":true});
            var Q19;
            Q19=makeQuery(id+"F1.opExtrude","CAP_EDGE",EDGE,{"disambiguationData":[OSD([sQuery(id+"F0.wireOp",EDGE,"E29.1.24")])],"isStart":true});
            var Q20;
            Q20=makeQuery(id+"F1.opExtrude","CAP_EDGE",EDGE,{"disambiguationData":[OSD([sQuery(id+"F0.wireOp",EDGE,"E29.1.0")])],"isStart":true});
            var Q21;
            {var subQ0=sQuery(id+"F0.wireOp",EDGE,"E29.1.2");Q21=makeQuery(id+"F1.opExtrude","CAP_EDGE",EDGE,{"disambiguationData":[OSD([subQ0]),TDD([makeQuery(id+"F0.imprint","IMPRINT",EDGE,{"disambiguationData":[TD([[makeQuery(id+"F0.imprint","INTERSECT",VERTEX,{"derivedFrom":[sQuery(id+"F0.wireOp",EDGE,"E29.1.0"),subQ0]}),-1.0]])],"derivedFrom":subQ0})])],"isStart":true});}
            var Q22;
            {var subQ0=sQuery(id+"F0.wireOp",EDGE,"E29.1.2");Q22=makeQuery(id+"F1.opExtrude","CAP_EDGE",EDGE,{"disambiguationData":[OSD([subQ0]),TDD([makeQuery(id+"F0.imprint","IMPRINT",EDGE,{"disambiguationData":[TD([[makeQuery(id+"F0.imprint","INTERSECT",VERTEX,{"derivedFrom":[subQ0,sQuery(id+"F0.wireOp",EDGE,"E29.1.15")]}),1.0]])],"derivedFrom":subQ0})])],"isStart":true});}
            var Q23;
            Q23=makeQuery(id+"F1.opExtrude","CAP_EDGE",EDGE,{"disambiguationData":[OSD([sQuery(id+"F0.wireOp",EDGE,"E29.1.17")])],"isStart":true});
            var Q24;
            {var subQ0=sQuery(id+"F0.wireOp",EDGE,"E3.0");Q24=makeQuery(id+"F1.opExtrude","CAP_EDGE",EDGE,{"disambiguationData":[OSD([subQ0]),TDD([makeQuery(id+"F0.imprint","IMPRINT",EDGE,{"disambiguationData":[TD([[makeQuery(id+"F0.imprint","INTERSECT",VERTEX,{"derivedFrom":[subQ0,sQuery(id+"F0.wireOp",EDGE,"E27.MirrorCS")]}),-1.0]])],"derivedFrom":subQ0})])],"isStart":true});}
            var Q25;
            {var subQ0=sQuery(id+"F0.wireOp",EDGE,"E3.0");Q25=makeQuery(id+"F1.opExtrude","CAP_EDGE",EDGE,{"disambiguationData":[OSD([subQ0]),TDD([makeQuery(id+"F0.imprint","IMPRINT",EDGE,{"disambiguationData":[TD([[makeQuery(id+"F0.imprint","INTERSECT",VERTEX,{"derivedFrom":[subQ0,sQuery(id+"F0.wireOp",EDGE,"E29.1.8")]}),-1.0]])],"derivedFrom":subQ0})])],"isStart":true});}
            var Q26;
            Q26=makeQuery(id+"F1.opExtrude","CAP_EDGE",EDGE,{"disambiguationData":[OSD([sQuery(id+"F0.wireOp",EDGE,"E27.MirrorCS")])],"isStart":true});
            var Q27;
            Q27=makeQuery(id+"F1.opExtrude","CAP_EDGE",EDGE,{"disambiguationData":[OSD([sQuery(id+"F0.wireOp",EDGE,"E15.trimOffspring")])],"isStart":true});
            var Q28;
            Q28=makeQuery(id+"F1.opExtrude","CAP_EDGE",EDGE,{"disambiguationData":[OSD([sQuery(id+"F0.wireOp",EDGE,"E13")])],"isStart":true});
            var Q29;
            Q29=makeQuery(id+"F1.opExtrude","CAP_EDGE",EDGE,{"disambiguationData":[OSD([sQuery(id+"F0.wireOp",EDGE,"E14")])],"isStart":true});
            var Q30;
            {var subQ0=sQuery(id+"F0.wireOp",EDGE,"E2.0");Q30=makeQuery(id+"F1.opExtrude","CAP_EDGE",EDGE,{"disambiguationData":[OSD([subQ0]),TDD([makeQuery(id+"F0.imprint","IMPRINT",EDGE,{"disambiguationData":[TD([[makeQuery(id+"F0.imprint","INTERSECT",VERTEX,{"derivedFrom":[subQ0,sQuery(id+"F0.wireOp",EDGE,"E19.1.0")]}),-1.0]])],"derivedFrom":subQ0})])],"isStart":true});}
            var Q31;
            Q31=makeQuery(id+"F1.opExtrude","CAP_EDGE",EDGE,{"disambiguationData":[OSD([sQuery(id+"F0.wireOp",EDGE,"E19.1.0")])],"isStart":true});
            var Q32;
            Q32=makeQuery(id+"F1.opExtrude","CAP_EDGE",EDGE,{"disambiguationData":[OSD([sQuery(id+"F0.wireOp",EDGE,"E19.1.1")])],"isStart":true});
            var Q33;
            {var subQ0=sQuery(id+"F0.wireOp",EDGE,"E2.0");Q33=makeQuery(id+"F1.opExtrude","CAP_EDGE",EDGE,{"disambiguationData":[OSD([subQ0]),TDD([makeQuery(id+"F0.imprint","IMPRINT",EDGE,{"disambiguationData":[TD([[makeQuery(id+"F0.imprint","INTERSECT",VERTEX,{"derivedFrom":[subQ0,sQuery(id+"F0.wireOp",EDGE,"E19.1.1")]}),1.0]])],"derivedFrom":subQ0})])],"isStart":true});}
            var Q34;
            Q34=makeQuery(id+"F1.opExtrude","CAP_EDGE",EDGE,{"disambiguationData":[OSD([sQuery(id+"F0.wireOp",EDGE,"E19.2.0")])],"isStart":true});
            var Q35;
            Q35=makeQuery(id+"F1.opExtrude","CAP_EDGE",EDGE,{"disambiguationData":[OSD([sQuery(id+"F0.wireOp",EDGE,"E19.2.1")])],"isStart":true});
            var Q36;
            {var subQ0=sQuery(id+"F0.wireOp",EDGE,"E2.0");Q36=makeQuery(id+"F1.opExtrude","CAP_EDGE",EDGE,{"disambiguationData":[OSD([subQ0]),TDD([makeQuery(id+"F0.imprint","IMPRINT",EDGE,{"disambiguationData":[TD([[makeQuery(id+"F0.imprint","INTERSECT",VERTEX,{"derivedFrom":[subQ0,sQuery(id+"F0.wireOp",EDGE,"E19.2.1")]}),1.0]])],"derivedFrom":subQ0})])],"isStart":true});}
            var Q37;
            Q37=makeQuery(id+"F1.opExtrude","CAP_EDGE",EDGE,{"disambiguationData":[OSD([sQuery(id+"F0.wireOp",EDGE,"E19.3.0")])],"isStart":true});
            var Q38;
            Q38=makeQuery(id+"F1.opExtrude","CAP_EDGE",EDGE,{"disambiguationData":[OSD([sQuery(id+"F0.wireOp",EDGE,"E19.3.1")])],"isStart":true});
            var Q39;
            {var subQ0=sQuery(id+"F0.wireOp",EDGE,"E2.0");Q39=makeQuery(id+"F1.opExtrude","CAP_EDGE",EDGE,{"disambiguationData":[OSD([subQ0]),TDD([makeQuery(id+"F0.imprint","IMPRINT",EDGE,{"disambiguationData":[TD([[makeQuery(id+"F0.imprint","INTERSECT",VERTEX,{"derivedFrom":[subQ0,sQuery(id+"F0.wireOp",EDGE,"E19.3.1")]}),1.0]])],"derivedFrom":subQ0})])],"isStart":true});}
            var Q40;
            Q40=makeQuery(id+"F1.opExtrude","CAP_EDGE",EDGE,{"disambiguationData":[OSD([sQuery(id+"F0.wireOp",EDGE,"E19.4.0")])],"isStart":true});
            var Q41;
            Q41=makeQuery(id+"F1.opExtrude","CAP_EDGE",EDGE,{"disambiguationData":[OSD([sQuery(id+"F0.wireOp",EDGE,"E19.4.1")])],"isStart":true});
            var Q42;
            {var subQ0=sQuery(id+"F0.wireOp",EDGE,"E2.0");Q42=makeQuery(id+"F1.opExtrude","CAP_EDGE",EDGE,{"disambiguationData":[OSD([subQ0]),TDD([makeQuery(id+"F0.imprint","IMPRINT",EDGE,{"disambiguationData":[TD([[makeQuery(id+"F0.imprint","INTERSECT",VERTEX,{"derivedFrom":[subQ0,sQuery(id+"F0.wireOp",EDGE,"E19.4.1")]}),1.0]])],"derivedFrom":subQ0})])],"isStart":true});}
            var Q43;
            Q43=makeQuery(id+"F1.opExtrude","CAP_EDGE",EDGE,{"disambiguationData":[OSD([sQuery(id+"F0.wireOp",EDGE,"E19.5.0")])],"isStart":true});
            var Q44;
            Q44=makeQuery(id+"F1.opExtrude","CAP_EDGE",EDGE,{"disambiguationData":[OSD([sQuery(id+"F0.wireOp",EDGE,"E19.5.1")])],"isStart":true});
            var Q45;
            {var subQ0=sQuery(id+"F0.wireOp",EDGE,"E2.0");Q45=makeQuery(id+"F1.opExtrude","CAP_EDGE",EDGE,{"disambiguationData":[OSD([subQ0]),TDD([makeQuery(id+"F0.imprint","IMPRINT",EDGE,{"disambiguationData":[TD([[makeQuery(id+"F0.imprint","INTERSECT",VERTEX,{"derivedFrom":[subQ0,sQuery(id+"F0.wireOp",EDGE,"E19.5.1")]}),1.0]])],"derivedFrom":subQ0})])],"isStart":true});}
            var Q46;
            Q46=makeQuery(id+"F1.opExtrude","CAP_EDGE",EDGE,{"disambiguationData":[OSD([sQuery(id+"F0.wireOp",EDGE,"E19.6.0")])],"isStart":true});
            var Q47;
            Q47=makeQuery(id+"F1.opExtrude","CAP_EDGE",EDGE,{"disambiguationData":[OSD([sQuery(id+"F0.wireOp",EDGE,"E19.6.1")])],"isStart":true});
            var Q48;
            Q48=makeQuery(id+"F1.opExtrude","CAP_EDGE",EDGE,{"disambiguationData":[OSD([sQuery(id+"F0.wireOp",EDGE,"E20.MirrorCS")])],"isStart":true});
            var Q49;
            {var subQ0=sQuery(id+"F0.wireOp",EDGE,"E3.0");Q49=makeQuery(id+"F1.opExtrude","CAP_EDGE",EDGE,{"disambiguationData":[OSD([subQ0]),TDD([makeQuery(id+"F0.imprint","IMPRINT",EDGE,{"disambiguationData":[TD([[makeQuery(id+"F0.imprint","INTERSECT",VERTEX,{"derivedFrom":[subQ0,sQuery(id+"F0.wireOp",EDGE,"E20.MirrorCS")]}),1.0]])],"derivedFrom":subQ0})])],"isStart":true});}
            var Q50;
            {var subQ0=sQuery(id+"F0.wireOp",EDGE,"E2.0");Q50=makeQuery(id+"F1.opExtrude","CAP_EDGE",EDGE,{"disambiguationData":[OSD([subQ0]),TDD([makeQuery(id+"F0.imprint","IMPRINT",EDGE,{"disambiguationData":[TD([[makeQuery(id+"F0.imprint","INTERSECT",VERTEX,{"derivedFrom":[subQ0,sQuery(id+"F0.wireOp",EDGE,"E20.MirrorCS")]}),-1.0]])],"derivedFrom":subQ0})])],"isStart":true});}
            var Q51;
            Q51=makeQuery(id+"F1.opExtrude","CAP_EDGE",EDGE,{"disambiguationData":[OSD([sQuery(id+"F0.wireOp",EDGE,"E29.2.8")])],"isStart":true});
            var Q52;
            Q52=makeQuery(id+"F1.opExtrude","CAP_EDGE",EDGE,{"disambiguationData":[OSD([sQuery(id+"F0.wireOp",EDGE,"E29.2.25")])],"isStart":true});
            var Q53;
            Q53=makeQuery(id+"F1.opExtrude","CAP_EDGE",EDGE,{"disambiguationData":[OSD([sQuery(id+"F0.wireOp",EDGE,"E29.2.10")])],"isStart":true});
            var Q54;
            Q54=makeQuery(id+"F1.opExtrude","CAP_EDGE",EDGE,{"disambiguationData":[OSD([sQuery(id+"F0.wireOp",EDGE,"E29.2.11")])],"isStart":true});
            var Q55;
            {var subQ0=sQuery(id+"F0.wireOp",EDGE,"E29.2.2");Q55=makeQuery(id+"F1.opExtrude","CAP_EDGE",EDGE,{"disambiguationData":[OSD([subQ0]),TDD([makeQuery(id+"F0.imprint","IMPRINT",EDGE,{"disambiguationData":[TD([[makeQuery(id+"F0.imprint","INTERSECT",VERTEX,{"derivedFrom":[subQ0,sQuery(id+"F0.wireOp",EDGE,"E29.2.11")]}),1.0]])],"derivedFrom":subQ0})])],"isStart":true});}
            var Q56;
            Q56=makeQuery(id+"F1.opExtrude","CAP_EDGE",EDGE,{"disambiguationData":[OSD([sQuery(id+"F0.wireOp",EDGE,"E29.2.12")])],"isStart":true});
            var Q57;
            Q57=makeQuery(id+"F1.opExtrude","CAP_EDGE",EDGE,{"disambiguationData":[OSD([sQuery(id+"F0.wireOp",EDGE,"E29.2.13")])],"isStart":true});
            var Q58;
            {var subQ0=sQuery(id+"F0.wireOp",EDGE,"E29.2.2");Q58=makeQuery(id+"F1.opExtrude","CAP_EDGE",EDGE,{"disambiguationData":[OSD([subQ0]),TDD([makeQuery(id+"F0.imprint","IMPRINT",EDGE,{"disambiguationData":[TD([[makeQuery(id+"F0.imprint","INTERSECT",VERTEX,{"derivedFrom":[subQ0,sQuery(id+"F0.wireOp",EDGE,"E29.2.13")]}),1.0]])],"derivedFrom":subQ0})])],"isStart":true});}
            var Q59;
            Q59=makeQuery(id+"F1.opExtrude","CAP_EDGE",EDGE,{"disambiguationData":[OSD([sQuery(id+"F0.wireOp",EDGE,"E29.2.14")])],"isStart":true});
            var Q60;
            Q60=makeQuery(id+"F1.opExtrude","CAP_EDGE",EDGE,{"disambiguationData":[OSD([sQuery(id+"F0.wireOp",EDGE,"E29.2.15")])],"isStart":true});
            var Q61;
            {var subQ0=sQuery(id+"F0.wireOp",EDGE,"E29.2.2");Q61=makeQuery(id+"F1.opExtrude","CAP_EDGE",EDGE,{"disambiguationData":[OSD([subQ0]),TDD([makeQuery(id+"F0.imprint","IMPRINT",EDGE,{"disambiguationData":[TD([[makeQuery(id+"F0.imprint","INTERSECT",VERTEX,{"derivedFrom":[subQ0,sQuery(id+"F0.wireOp",EDGE,"E29.2.15")]}),1.0]])],"derivedFrom":subQ0})])],"isStart":true});}
            var Q62;
            Q62=makeQuery(id+"F1.opExtrude","CAP_EDGE",EDGE,{"disambiguationData":[OSD([sQuery(id+"F0.wireOp",EDGE,"E29.2.17")])],"isStart":true});
            var Q63;
            Q63=makeQuery(id+"F1.opExtrude","CAP_EDGE",EDGE,{"disambiguationData":[OSD([sQuery(id+"F0.wireOp",EDGE,"E29.2.16")])],"isStart":true});
            var Q64;
            {var subQ0=sQuery(id+"F0.wireOp",EDGE,"E29.2.2");Q64=makeQuery(id+"F1.opExtrude","CAP_EDGE",EDGE,{"disambiguationData":[OSD([subQ0]),TDD([makeQuery(id+"F0.imprint","IMPRINT",EDGE,{"disambiguationData":[TD([[makeQuery(id+"F0.imprint","INTERSECT",VERTEX,{"derivedFrom":[subQ0,sQuery(id+"F0.wireOp",EDGE,"E29.2.16")]}),1.0]])],"derivedFrom":subQ0})])],"isStart":true});}
            var Q65;
            Q65=makeQuery(id+"F1.opExtrude","CAP_EDGE",EDGE,{"disambiguationData":[OSD([sQuery(id+"F0.wireOp",EDGE,"E29.2.20")])],"isStart":true});
            var Q66;
            Q66=makeQuery(id+"F1.opExtrude","CAP_EDGE",EDGE,{"disambiguationData":[OSD([sQuery(id+"F0.wireOp",EDGE,"E29.2.19")])],"isStart":true});
            var Q67;
            {var subQ0=sQuery(id+"F0.wireOp",EDGE,"E29.2.2");Q67=makeQuery(id+"F1.opExtrude","CAP_EDGE",EDGE,{"disambiguationData":[OSD([subQ0]),TDD([makeQuery(id+"F0.imprint","IMPRINT",EDGE,{"disambiguationData":[TD([[makeQuery(id+"F0.imprint","INTERSECT",VERTEX,{"derivedFrom":[subQ0,sQuery(id+"F0.wireOp",EDGE,"E29.2.19")]}),1.0]])],"derivedFrom":subQ0})])],"isStart":true});}
            var Q68;
            Q68=makeQuery(id+"F1.opExtrude","CAP_EDGE",EDGE,{"disambiguationData":[OSD([sQuery(id+"F0.wireOp",EDGE,"E29.2.21")])],"isStart":true});
            var Q69;
            Q69=makeQuery(id+"F1.opExtrude","CAP_EDGE",EDGE,{"disambiguationData":[OSD([sQuery(id+"F0.wireOp",EDGE,"E29.2.22")])],"isStart":true});
            var Q70;
            {var subQ0=sQuery(id+"F0.wireOp",EDGE,"E29.2.2");Q70=makeQuery(id+"F1.opExtrude","CAP_EDGE",EDGE,{"disambiguationData":[OSD([subQ0]),TDD([makeQuery(id+"F0.imprint","IMPRINT",EDGE,{"disambiguationData":[TD([[makeQuery(id+"F0.imprint","INTERSECT",VERTEX,{"derivedFrom":[subQ0,sQuery(id+"F0.wireOp",EDGE,"E29.2.22")]}),1.0]])],"derivedFrom":subQ0})])],"isStart":true});}
            var Q71;
            Q71=makeQuery(id+"F1.opExtrude","CAP_EDGE",EDGE,{"disambiguationData":[OSD([sQuery(id+"F0.wireOp",EDGE,"E29.2.23")])],"isStart":true});
            var Q72;
            Q72=makeQuery(id+"F1.opExtrude","CAP_EDGE",EDGE,{"disambiguationData":[OSD([sQuery(id+"F0.wireOp",EDGE,"E29.2.24")])],"isStart":true});
            var Q73;
            {var subQ0=sQuery(id+"F0.wireOp",EDGE,"E29.2.2");Q73=makeQuery(id+"F1.opExtrude","CAP_EDGE",EDGE,{"disambiguationData":[OSD([subQ0]),TDD([makeQuery(id+"F0.imprint","IMPRINT",EDGE,{"disambiguationData":[TD([[makeQuery(id+"F0.imprint","INTERSECT",VERTEX,{"derivedFrom":[sQuery(id+"F0.wireOp",EDGE,"E29.2.0"),subQ0]}),-1.0]])],"derivedFrom":subQ0})])],"isStart":true});}
            var Q74;
            Q74=makeQuery(id+"F1.opExtrude","CAP_EDGE",EDGE,{"disambiguationData":[OSD([sQuery(id+"F0.wireOp",EDGE,"E29.2.0")])],"isStart":true});
            fillet(context, id + "F3", {"entities" : qUnion([Q0, Q1, Q2, Q3, Q4, Q5, Q6, Q7, Q8, Q9, Q10, Q11, Q12, Q13, Q14, Q15, Q16, Q17, Q18, Q19, Q20, Q21, Q22, Q23, Q24, Q25, Q26, Q27, Q28, Q29, Q30, Q31, Q32, Q33, Q34, Q35, Q36, Q37, Q38, Q39, Q40, Q41, Q42, Q43, Q44, Q45, Q46, Q47, Q48, Q49, Q50, Q51, Q52, Q53, Q54, Q55, Q56, Q57, Q58, Q59, Q60, Q61, Q62, Q63, Q64, Q65, Q66, Q67, Q68, Q69, Q70, Q71, Q72, Q73, Q74]), "radius" : 2 * mm, "tangentPropagation" : true, "allowEdgeOverflow" : false});
        }
    });
